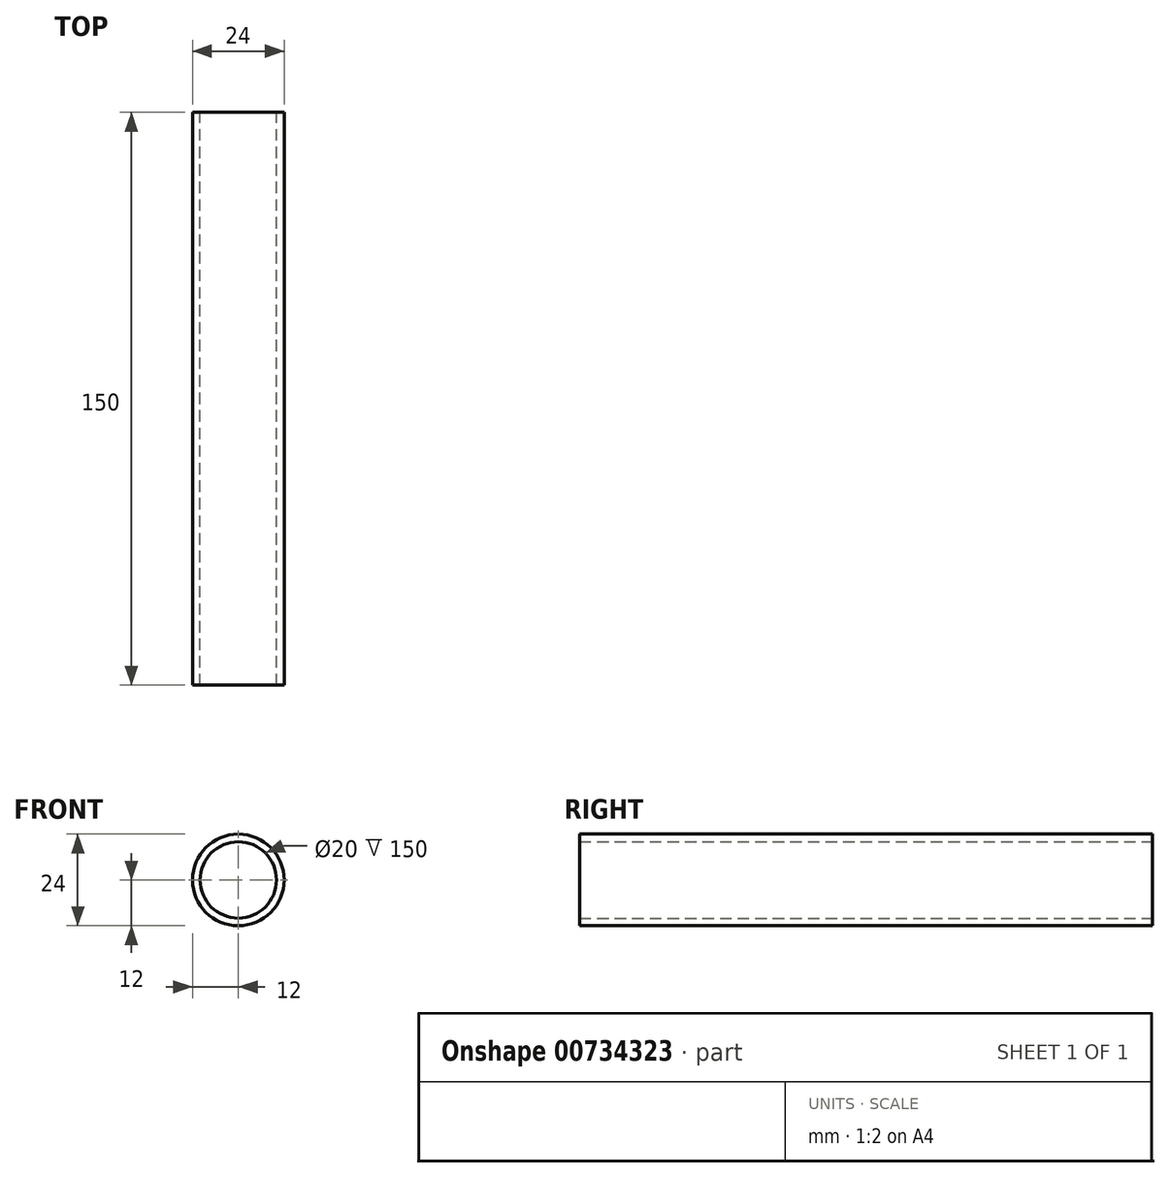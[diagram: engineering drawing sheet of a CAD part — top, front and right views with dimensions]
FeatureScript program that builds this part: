
annotation { "Feature Type Name" : "Feature", "Feature Type Description" : "" }
export const myFeature = defineFeature(function(context is Context, id is Id, definition is map)
    precondition{}
    {
        {
            var Q0;
            Q0=qCreatedBy(makeId("Front.planeOp"),FACE);
            var sketch = newSketch(context, id + "F0", { "sketchPlane" : qUnion([Q0])});
            skCircle(sketch, "E0", {"center": v(0, 0) * mm, "radius": 10 * mm});
            skCircle(sketch, "E1.0", {"center": v(0, 0) * mm, "radius": 12 * mm});
            skSolve(sketch);
        }
        {
            var Q0;
            Q0 = qSketchRegion(id + "F0", true);
            extrude(context, id + "F1", {"entities" : qUnion([Q0]), "depth" : 150 * mm, "offsetDistance" : 25 * mm});
        }
    });
